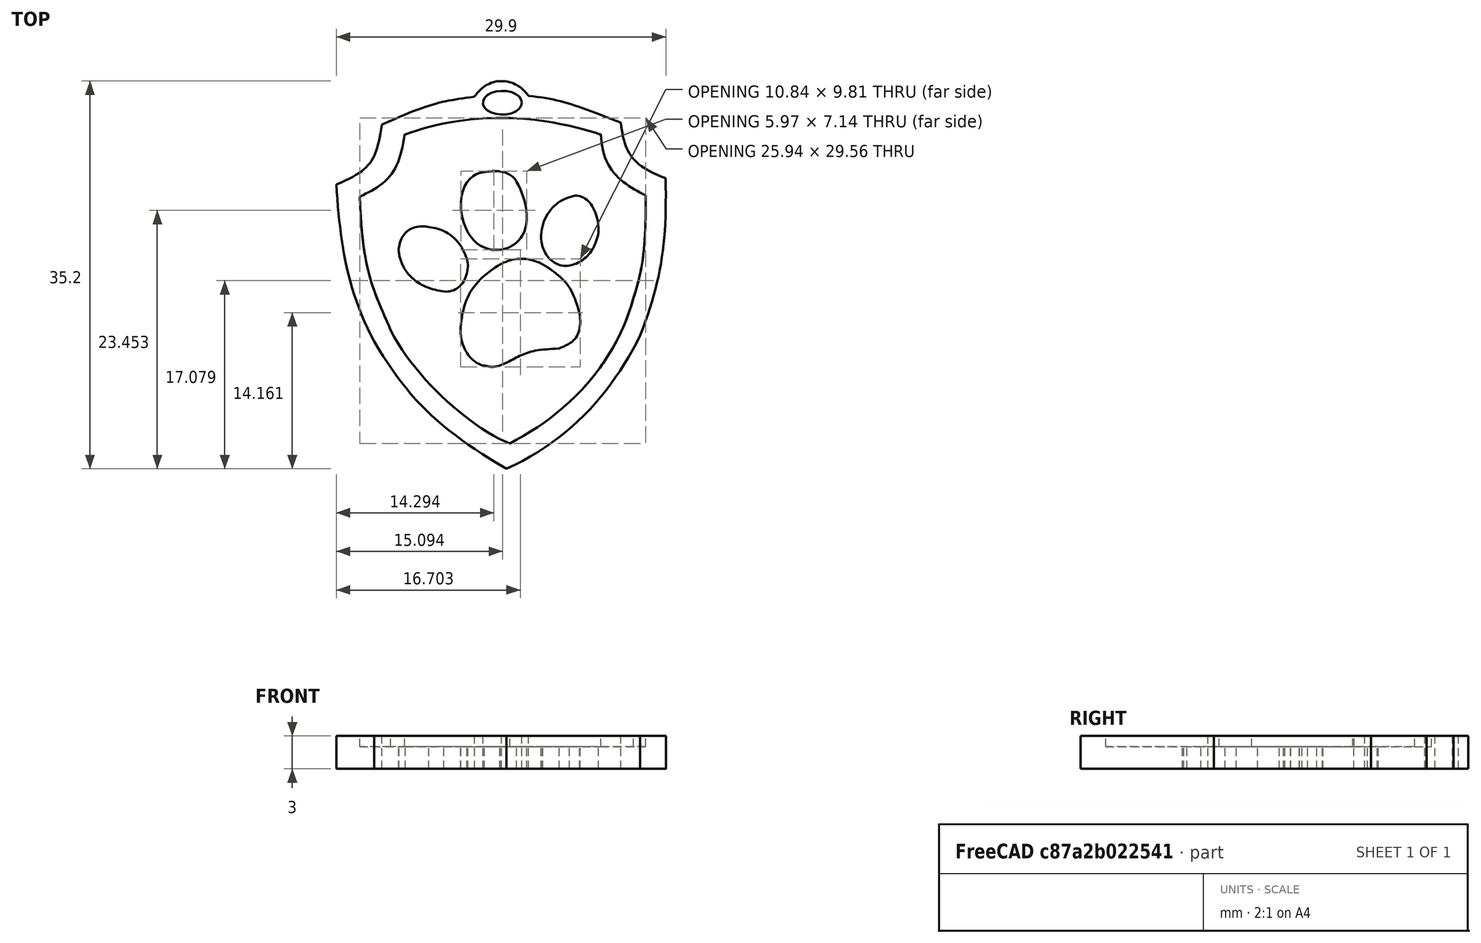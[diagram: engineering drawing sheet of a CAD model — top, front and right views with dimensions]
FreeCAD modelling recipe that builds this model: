
FCSTD DOCUMENT  (FreeCAD 0.14R3702 (Git))
Label: patrulla
License: CC-BY 3.0
LicenseURL: http://creativecommons.org/licenses/by/3.0/
objects: Part::Feature×8, Part::Extrusion×8, Part::Cut×3, Part::MultiFuse×2
note: 21 computed .brp shape members not serialized (recipe doc carries the construction recipe); baked Part::Feature solids carry a one-line shape summary decoded from their .brp

FEATURE [Part::Feature] path4766
  shape: bbox 30.03 x 35.24 x 2e-07 mm, 0 faces, 0 solids (baked)
FEATURE [Part::Feature] path4768
  shape: bbox 26 x 29.86 x 2e-07 mm, 0 faces, 0 solids (baked)
FEATURE [Part::Feature] path4770
  shape: bbox 6.588 x 6.193 x 2e-07 mm, 0 faces, 0 solids (baked)
FEATURE [Part::Feature] path4772
  shape: bbox 7.078 x 7.668 x 2e-07 mm, 0 faces, 0 solids (baked)
FEATURE [Part::Feature] path4774
  shape: bbox 5.478 x 6.662 x 2e-07 mm, 0 faces, 0 solids (baked)
FEATURE [Part::Feature] path4776
  shape: bbox 11.27 x 9.981 x 2e-07 mm, 0 faces, 0 solids (baked)
FEATURE [Part::Feature] path4788
  shape: bbox 3.794 x 2.314 x 2e-07 mm, 1 faces, 0 solids (baked)
FEATURE [Part::Extrusion] Extrude
  Base = -> path4770
  Dir = (0,0,6)
  Solid = true
FEATURE [Part::Extrusion] Extrude001
  Base = -> path4776
  Dir = (0,0,6)
  Solid = true
FEATURE [Part::Extrusion] Extrude002
  Base = -> path4774
  Dir = (0,0,6)
  Solid = true
FEATURE [Part::Extrusion] Extrude004
  Base = -> path4772
  Dir = (0,0,6)
  Solid = true
FEATURE [Part::MultiFuse] Fusion
  Placement = pos=(0,0,-1) rot=(0,0,1;0rad)
  Shapes = -> [Extrude,Extrude001,Extrude002,Extrude004]
FEATURE [Part::Extrusion] Extrude005
  Base = -> path4788
  Dir = (0,0,6)
  Placement = pos=(0,0,-1) rot=(0,0,1;0rad)
  Solid = false
FEATURE [Part::Feature] path
  Placement = pos=(0,0,-1) rot=(0,0,1;0rad)
  shape: bbox 26 x 29.86 x 2e-07 mm, 0 faces, 0 solids (baked)
FEATURE [Part::Extrusion] Extrude006
  Base = -> path
  Dir = (0,0,5)
  Solid = true
FEATURE [Part::Extrusion] Extrude007
  Base = -> path4766
  Dir = (0,0,3)
  Solid = true
FEATURE [Part::Cut] Cut
  Base = -> Extrude007
  Tool = -> Extrude006
FEATURE [Part::Extrusion] Extrude008
  Base = -> path4768
  Dir = (0,0,2)
  Solid = true
FEATURE [Part::Cut] Cut001
  Base = -> Extrude008
  Tool = -> Fusion
FEATURE [Part::Cut] Cut002
  Base = -> Cut
  Tool = -> Extrude005
FEATURE [Part::MultiFuse] Fusion001
  Shapes = -> [Cut001,Cut002]
